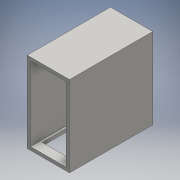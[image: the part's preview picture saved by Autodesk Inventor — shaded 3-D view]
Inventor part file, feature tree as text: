
AUTODESK INVENTOR PART (.ipt)
format: ipt  version: 2016 (Build 200138000, 138)  size: 144,896 bytes
history: native  units: mm
features: sketch x6, extrude x5
ambient origin geometry x8: Origin, YZ Plane, XZ Plane, XY Plane, X Axis, Y Axis, Z Axis, Center Point
bodies: Solid1 (feature_tree)
feature tree (11):
  extrude  "Extrusion1"  Depth=520.0mm
  extrude  "Extrusion2"  Depth=583.0mm TaperAngle=0.0deg
  extrude  "Extrusion3"  Depth=440.0mm
  sketch  "Sketch4"  dims[d7=77.0mm d8=38.0mm]
  extrude  "Extrusion4"  Depth=38.0mm
  extrude  "Extrusion5"  Depth=70.0mm
  sketch  "Sketch1"  dims[d0=250.0mm d1=520.0mm]
  sketch  "Sketch2"  dims[d2=23.0mm d3=583.0mm d4=0.0mm]
  sketch  "Sketch3"  dims[d5=220.0mm d6=440.0mm]
  sketch  "Sketch5"  dims[d9=583.0mm d10=0.0mm d11=70.0mm]
  sketch  "Sketch6"  dims[d12=80.0mm d13=430.0mm d14=143.0mm d15=583.0mm d16=0.0mm d17=47.0mm d18=583.0mm d19=0.0mm d20=16.0mm d21=170.0mm d22=45.0mm d23=16.0mm d24=170.0mm d25=45.0mm d26=10.0mm d27=0.0mm]
